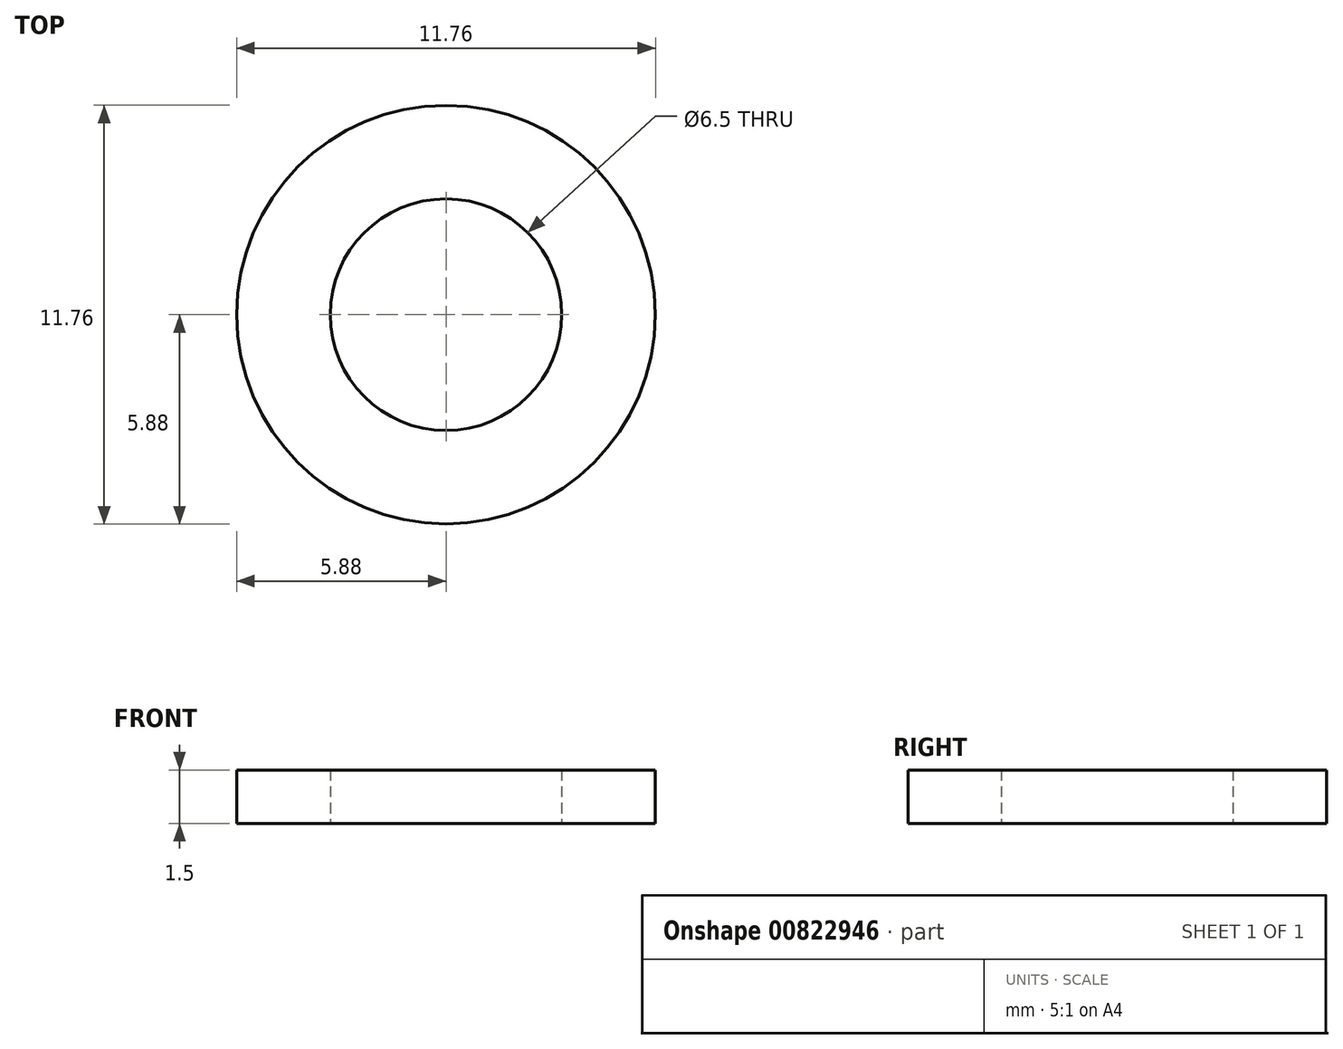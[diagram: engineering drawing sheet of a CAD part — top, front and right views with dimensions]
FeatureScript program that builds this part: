
annotation { "Feature Type Name" : "Feature", "Feature Type Description" : "" }
export const myFeature = defineFeature(function(context is Context, id is Id, definition is map)
    precondition{}
    {
        {
            var Q0;
            Q0=qCreatedBy(makeId("Top.planeOp"),FACE);
            var sketch = newSketch(context, id + "F0", { "sketchPlane" : qUnion([Q0])});
            skCircle(sketch, "E0", {"center": v(0, 0) * mm, "radius": 5.88 * mm});
            skCircle(sketch, "E1", {"center": v(0, 0) * mm, "radius": 3.25 * mm});
            skSolve(sketch);
        }
        {
            var Q0;
            Q0=qSketchRegion(id+"F0",true);
            extrude(context, id + "F1", {"entities" : qUnion([Q0]), "depth" : 1.5 * mm, "offsetDistance" : 25 * mm});
        }
    });
